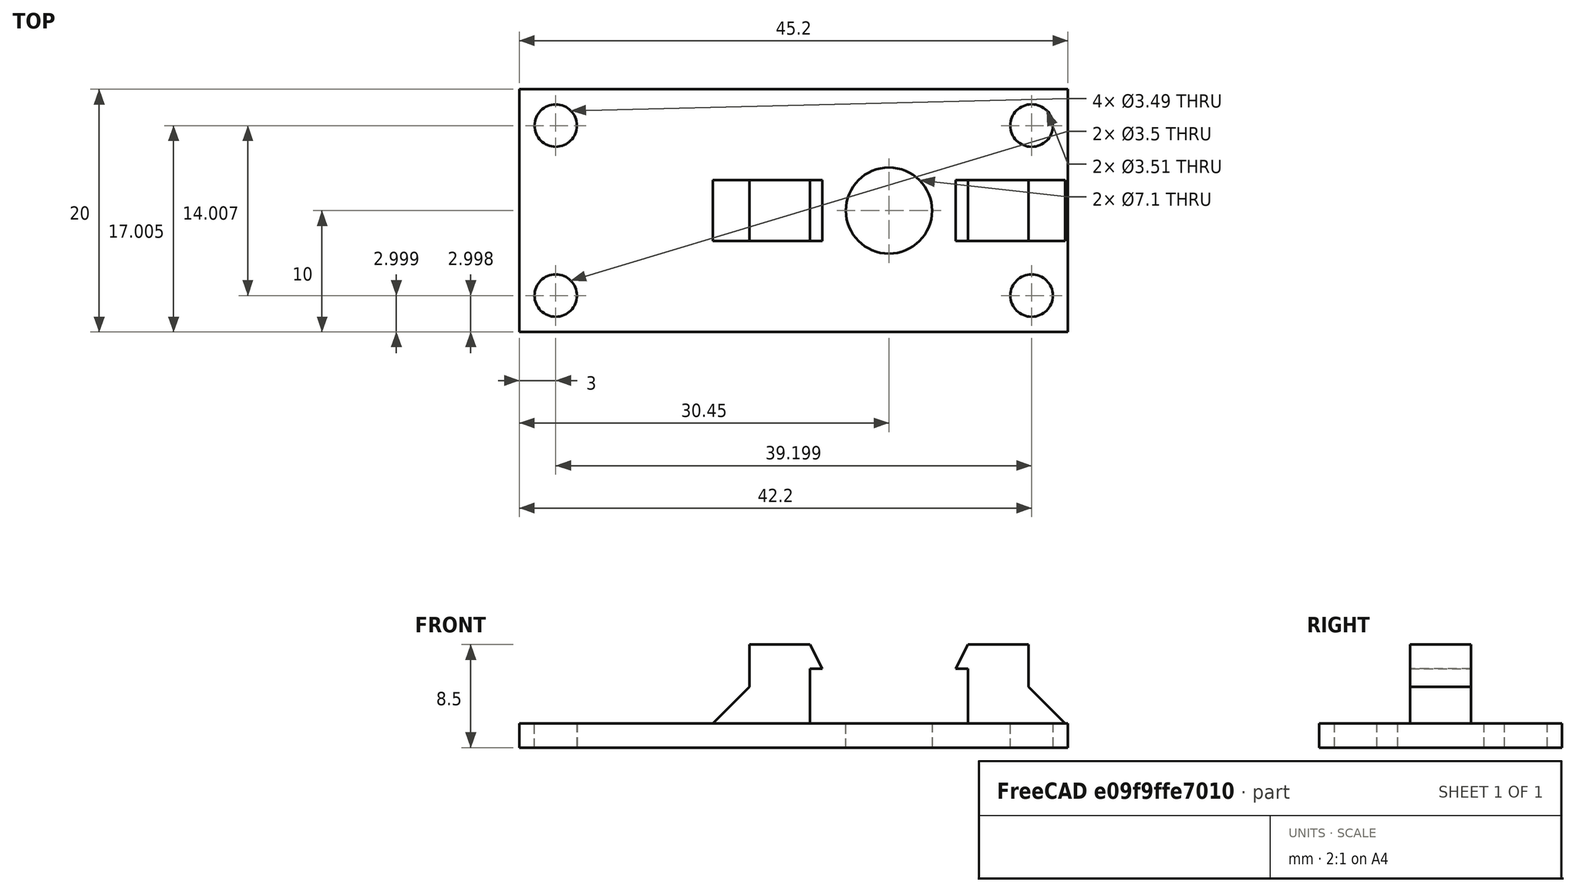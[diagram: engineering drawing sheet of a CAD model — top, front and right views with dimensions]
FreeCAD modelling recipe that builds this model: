
FCSTD DOCUMENT  (FreeCAD 0.17R13522 (Git))
Label: base_inferior_con_soportes_v2
License: CreativeCommons Attribution-ShareAlike
LicenseURL: http://creativecommons.org/licenses/by-sa/4.0/
objects: Part::Part2DObjectPython×9, Part::Extrusion×8, Part::Cut×5, Part::Fuse×4, Part::Feature×3, Part::Chamfer×2, Part::Box×1, Part::FeaturePython×1
note: 33 computed .brp shape members not serialized (recipe doc carries the construction recipe); baked Part::Feature solids carry a one-line shape summary decoded from their .brp

FEATURE [Part::Box] Box  label="placa base"
  AttacherType = Attacher::AttachEngine3D
  Height = 2
  Length = 45.2
  Width = 20
FEATURE [Part::Part2DObjectPython] Circle  label="taladro inferior izquierdo"  # Draft 2D object (typed FeaturePython)
  FirstAngle = 0
  LastAngle = 0
  MakeFace = false
  Placement = pos=(3,2.99873,2) rot=(0,0,1;3.14159rad)
  Radius = 1.74945
FEATURE [Part::Part2DObjectPython] Circle001  label="taladro inferior derecho"  # Draft 2D object (typed FeaturePython)
  FirstAngle = 0
  LastAngle = 0
  MakeFace = false
  Placement = pos=(42.1991,2.99781,2) rot=(0,0,1;3.14159rad)
  Radius = 1.7464
FEATURE [Part::Part2DObjectPython] Circle002  label="taladro superior derecho"  # Draft 2D object (typed FeaturePython)
  FirstAngle = 0
  LastAngle = 0
  MakeFace = false
  Placement = pos=(42.2,17.005,2) rot=(0,0,1;3.14159rad)
  Radius = 1.75369
FEATURE [Part::Part2DObjectPython] Circle003  label="taladro superior izquierdo"  # Draft 2D object (typed FeaturePython)
  FirstAngle = 0
  LastAngle = 0
  MakeFace = false
  Placement = pos=(3,17.005,2) rot=(0,0,1;3.14159rad)
  Radius = 1.74699
FEATURE [Part::Extrusion] Extrude
  Base = -> Circle003
  Dir = (0,0,1)
  DirMode = 2
  FaceMakerClass = Part::FaceMakerBullseye
  LengthFwd = 10
  LengthRev = 0
  Placement = pos=(0,0,-5) rot=(0,0,1;0rad)
  Solid = true
  Symmetric = false
FEATURE [Part::Extrusion] Extrude001
  Base = -> Circle
  Dir = (0,0,1)
  DirMode = 2
  FaceMakerClass = Part::FaceMakerBullseye
  LengthFwd = 10
  LengthRev = 0
  Placement = pos=(0,0,-5) rot=(0,0,1;0rad)
  Solid = true
  Symmetric = false
FEATURE [Part::Extrusion] Extrude002
  Base = -> Circle001
  Dir = (0,0,1)
  DirMode = 2
  FaceMakerClass = Part::FaceMakerBullseye
  LengthFwd = 10
  LengthRev = 0
  Placement = pos=(0,0,-5) rot=(0,0,1;0rad)
  Solid = true
  Symmetric = false
FEATURE [Part::Extrusion] Extrude003
  Base = -> Circle002
  Dir = (0,0,1)
  DirMode = 2
  FaceMakerClass = Part::FaceMakerBullseye
  LengthFwd = 10
  LengthRev = 0
  Placement = pos=(0,0,-5) rot=(0,0,1;0rad)
  Solid = true
  Symmetric = false
FEATURE [Part::Cut] Cut
  Base = -> Box
  Refine = true
  Tool = -> Extrude001
FEATURE [Part::Cut] Cut001
  Base = -> Cut
  Refine = true
  Tool = -> Extrude
FEATURE [Part::Part2DObjectPython] Circle004  # Draft 2D object (typed FeaturePython)
  FirstAngle = 0
  LastAngle = 0
  MakeFace = false
  Placement = pos=(30.45,10,2) rot=(0,0,1;3.14159rad)
  Radius = 3.55
FEATURE [Part::Extrusion] Extrude004
  Base = -> Circle004
  Dir = (0,0,1)
  DirMode = 2
  FaceMakerClass = Part::FaceMakerBullseye
  LengthFwd = 10
  LengthRev = 0
  Placement = pos=(0,0,-4) rot=(0,0,1;0rad)
  Solid = true
  Symmetric = false
FEATURE [Part::Cut] Cut002
  Base = -> Cut001
  Refine = true
  Tool = -> Extrude002
FEATURE [Part::Cut] Cut003  label="base con taladros en esquina"
  Base = -> Cut002
  Refine = true
  Tool = -> Extrude003
FEATURE [Part::Feature] Clone002_solid  label="Clone002 (Solid)"
  Placement = pos=(22.6,40,0) rot=(0,0,1;0rad)
  shape: bbox 6 x 5 x 8 mm, 10 faces (baked)
FEATURE [Part::Feature] Clone001001  label="Clone003"
  Placement = pos=(38.3,10,0) rot=(0,0,1;0rad)
  shape: bbox 6 x 5 x 8 mm, 10 faces (baked)
FEATURE [Part::Feature] Cut004_solid001001  label="base con agujeros (Solid)002"
  shape: bbox 45.2 x 20 x 2 mm, 11 faces (baked)
FEATURE [Part::Cut] Cut004  label="base con agujeros"
  Base = -> Cut003
  Refine = true
  Tool = -> Extrude004
FEATURE [Part::Part2DObjectPython] Rectangle001  # Draft 2D object (typed FeaturePython)
  ChamferSize = 0
  Columns = 1
  FilletRadius = 0
  Height = 5
  Length = -5
  MakeFace = false
  Placement = pos=(36.95,12.5,2) rot=(0,0,1;3.14159rad)
  Rows = 1
FEATURE [Part::Part2DObjectPython] Rectangle  # Draft 2D object (typed FeaturePython)
  ChamferSize = 0
  Columns = 1
  FilletRadius = 0
  Height = 5
  Length = 5
  MakeFace = false
  Placement = pos=(23.95,12.5,2) rot=(0,0,1;3.14159rad)
  Rows = 1
FEATURE [Part::Fuse] Fusion
  Base = -> Clone002_solid
  Refine = true
  Tool = -> Cut004_solid001001
FEATURE [Part::Chamfer] Chamfer
  Base = -> Fusion
  Edges = 1 edges r=3: [Edge24]
FEATURE [Part::Fuse] Fusion001
  Base = -> Clone001001
  Refine = true
  Tool = -> Chamfer
FEATURE [Part::Chamfer] Chamfer001
  Base = -> Fusion001
  Edges = 1 edges r=3: [Edge24]
FEATURE [Part::Part2DObjectPython] Rectangle002  # Draft 2D object (typed FeaturePython)
  ChamferSize = 0
  Columns = 1
  FilletRadius = 0
  Height = 1.78237
  Length = 0.0235148
  MakeFace = true
  Placement = pos=(36.942,7.5,6.49553) rot=(1,0,0;1.5708rad)
  Rows = 1
  Support = -> [Chamfer001]
FEATURE [Part::Extrusion] Extrude005
  Base = -> Rectangle002
  Dir = (0,-1,0)
  DirMode = 2
  FaceMakerClass = Part::FaceMakerBullseye
  LengthFwd = 5
  LengthRev = 0
  Placement = pos=(0,5,0) rot=(0,0,1;0rad)
  Solid = false
  Symmetric = false
FEATURE [Part::Fuse] Fusion002
  Base = -> Chamfer001
  Refine = true
  Tool = -> Extrude005
FEATURE [Part::Part2DObjectPython] Rectangle003  # Draft 2D object (typed FeaturePython)
  ChamferSize = 0
  Columns = 1
  FilletRadius = 0
  Height = 1.79673
  Length = 0.26
  MakeFace = true
  Placement = pos=(23.7023,7.5,6.49553) rot=(1,0,0;1.5708rad)
  Rows = 1
FEATURE [Part::Extrusion] Extrude006
  Base = -> Rectangle003
  Dir = (0,-1,0)
  DirMode = 2
  FaceMakerClass = Part::FaceMakerBullseye
  LengthFwd = 5
  LengthRev = 0
  Placement = pos=(0,5,0) rot=(0,0,1;0rad)
  Solid = false
  Symmetric = false
FEATURE [Part::Extrusion] Extrude007
  Base = -> Rectangle003
  Dir = (0,-1,0)
  DirMode = 2
  FaceMakerClass = Part::FaceMakerBullseye
  LengthFwd = 5
  LengthRev = 0
  Placement = pos=(0,5,0) rot=(0,0,1;0rad)
  Solid = false
  Symmetric = false
FEATURE [Part::FeaturePython] BooleanFragments  # WARN: FeaturePython — macro-defined, semantics opaque (R4)
  Mode = 0
  Objects = -> [Fusion002,Extrude006]
  Tolerance = 0
FEATURE [Part::Fuse] Fusion003
  Base = -> Extrude007
  Refine = true
  Tool = -> BooleanFragments
